# Revit family: Deca_Torneira Decalux Mesa Acionamento com Sensor 110V-220V_1180
name_source: partatom
category: Plumbing Fixtures
units: mm (PartAtom-declared; Revit-internal decimal feet)

## family parameters
Cut with Voids When Loaded = No
Host = Face
Part Type = Normal
Room Calculation Point = No
Round Connector Dimension = Use Radius
Shared = No

## types (1)
- 1180.C_Cromado CR10
    Acompanha o Produto = Acompanha restritor de vazão 5L/Min
    Aprovado por = quattroD
    Atendimento ao Cliente = 0800-0117073
    CWFU = 0
    Categoria = USO PUBLICO
    Composição Anel Vedação = -
    Composição Assento = -
    Composição Básica = Liga de Cobre (bronze e latão),Plásticos de Engenharia,Elastômeros,Eletrônicos
    Composição Componente = -
    Consumo = 6 L/min
    Cor Interna = -
    Cor Principal = Cromado
    Cor Secundária = -
    Cores Componente = -
    Criado por = quattroD
    Código Pai = 1180
    Default Elevation = 0 m
    Description = Torneira de mesa com sensor bivolt para lavatório
    Diâmetro Água Fria = 0.02 m
    Flow Pressure = 0.00 psi
    HWFU = 0
    Informações Complementares = -
    Itens de Instalação = -
    Linha = Decalux
    Manufacturer = Deca
    Material = Deca_Cromado
    Model = 1180.C
    Norma = NBR9050
    Peso Líquido (Kg) = 1.603
    Pressão = 2 A 40 mca
    Pressão máx. funcionamento = 40 MCA
    Pressão mín. Aquec. Acúmulo = -
    Pressão mín. Aquec. Passagem = -
    Pressão mín. funcionamento = 2 MCA
    Raio Água Fria = 0.01 m
    Saída de Esgoto = -
    Segmento = Banheiro Médio
    Tipo de dispositivo economizador = Sim
    Tipo de mecanismo utilizado = Solenóide
    Tipo de rosca de entrada = BSP NBR 8133
    Tipo de rosca de saída = -
    URL = www.deca.com.br
    Vazão na Pressão máx. (L/min) = 6
    Vazão na Pressão mín. (L/min) = 2.6

note: source unit labels omitted for Vazão na Pressão máx. (L/min), Vazão na Pressão mín. (L/min) — the stored unit's dimension contradicts the parameter name (converter mislabeling)

## geometry (parser evidence)
native form markers: Sweep x2
no freeform markers — native parametric forms only
